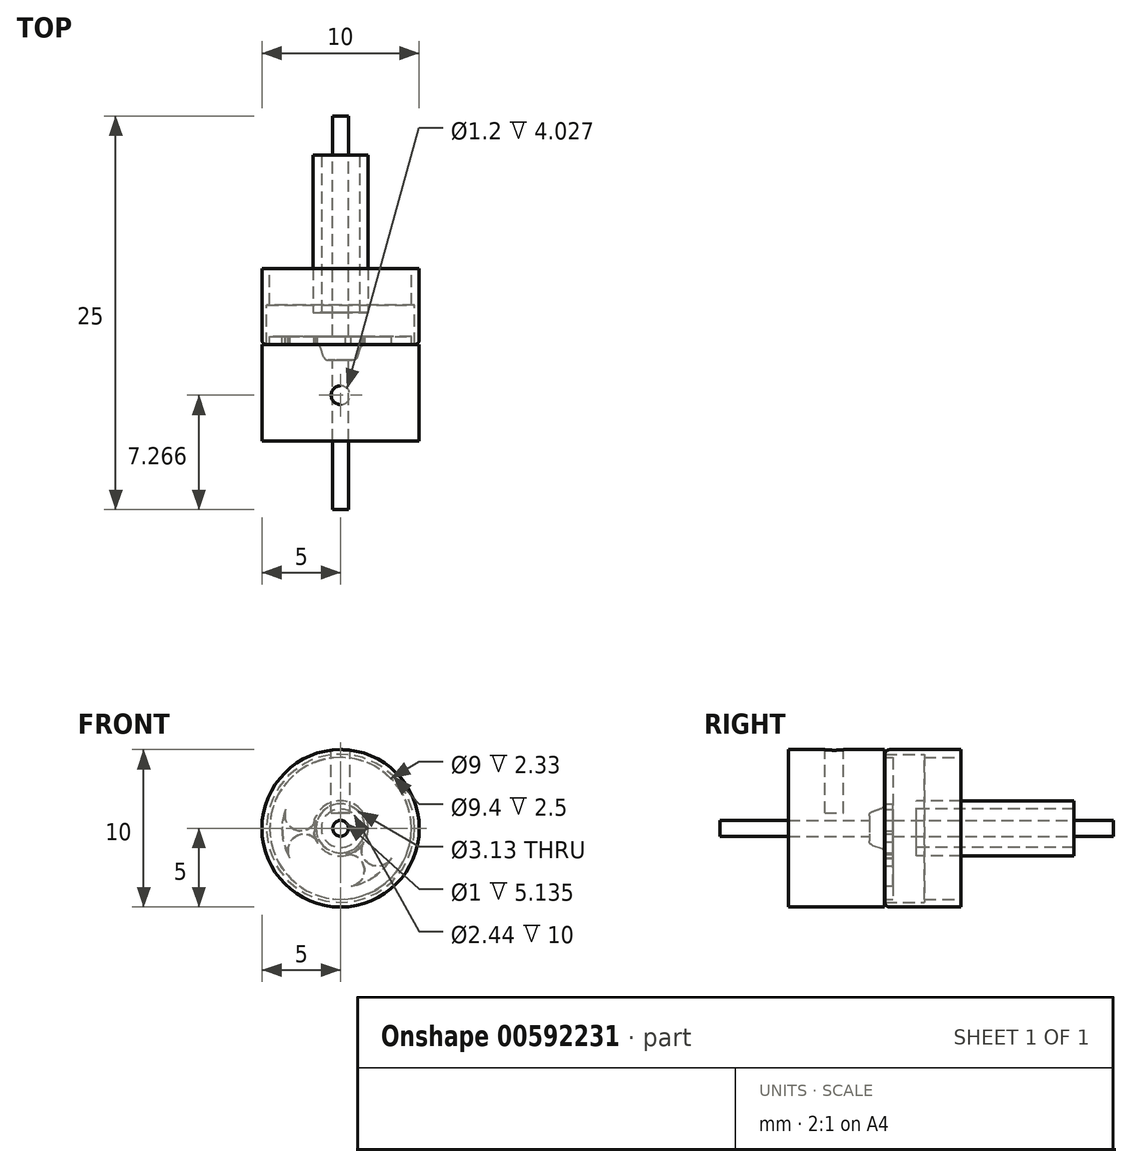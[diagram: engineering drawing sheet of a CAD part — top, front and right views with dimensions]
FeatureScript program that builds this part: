
annotation { "Feature Type Name" : "Feature", "Feature Type Description" : "" }
export const myFeature = defineFeature(function(context is Context, id is Id, definition is map)
    precondition{}
    {
        {
            var Q0;
            Q0=qCreatedBy(makeId("Right.planeOp"),FACE);
            var sketch = newSketch(context, id + "F0", { "sketchPlane" : qUnion([Q0])});
            skLineSegment(sketch, "E0", {"start": v(-3.01, 0) * mm, "end": v(-3.01, 1) * mm});
            skLineSegment(sketch, "E1", {"start": v(-3.01, 1) * mm, "end": v(-2.01, 1.35) * mm});
            skLineSegment(sketch, "E2", {"start": v(-2.01, 1.35) * mm, "end": v(-2.01, 5) * mm});
            skLineSegment(sketch, "E3", {"start": v(-2.01, 5) * mm, "end": v(2.82, 5) * mm});
            skLineSegment(sketch, "E4", {"start": v(2.82, 5) * mm, "end": v(2.82, 4.5) * mm});
            skLineSegment(sketch, "E5", {"start": v(2.82, 4.5) * mm, "end": v(-1.51, 4.5) * mm});
            skLineSegment(sketch, "E6", {"start": v(-1.51, 4.5) * mm, "end": v(-1.51, 0) * mm});
            skLineSegment(sketch, "E7", {"start": v(-1.51, 0) * mm, "end": v(-3.01, 0) * mm});
            skSolve(sketch);
        }
        {
            var Q0;
            Q0 = qSketchRegion(id + "F0", true);
            var Q1;
            Q1=sQuery(id+"F0.wireOp",EDGE,"E7");
            revolve(context, id + "F1", {"entities" : qUnion([Q0]), "axis" : qUnion([Q1]), "revolveType" : RevolveType.FULL});
        }
        {
            var Q0;
            Q0=makeQuery(id+"F1.opRevolve","SWEPT_EDGE",EDGE,{"disambiguationData":[OSD([sQuery(id+"F0.wireOp",EDGE,"E2"),sQuery(id+"F0.wireOp",EDGE,"E3")])]});
            var Q1;
            Q1=makeQuery(id+"F1.opRevolve","SWEPT_EDGE",EDGE,{"disambiguationData":[OSD([sQuery(id+"F0.wireOp",EDGE,"E1"),sQuery(id+"F0.wireOp",EDGE,"E2")])]});
            var Q2;
            Q2=makeQuery(id+"F1.opRevolve","SWEPT_EDGE",EDGE,{"disambiguationData":[OSD([sQuery(id+"F0.wireOp",EDGE,"E0"),sQuery(id+"F0.wireOp",EDGE,"E1")])]});
            fillet(context, id + "F2", {"entities" : qUnion([Q0, Q1, Q2]), "radius" : .3 * mm, "tangentPropagation" : true, "allowEdgeOverflow" : false});
        }
        {
            var Q0;
            Q0=makeQuery(id+"F1.opRevolve","SWEPT_FACE",FACE,{"disambiguationData":[OSD([sQuery(id+"F0.wireOp",EDGE,"E2")])]});
            var sketch = newSketch(context, id + "F3", { "sketchPlane" : qUnion([Q0])});
            skCircle(sketch, "E8", {"center": v(0, 2.66) * mm, "radius": 1.02 * mm});
            skCircle(sketch, "E9.1.0", {"center": v(2.04, 1.71) * mm, "radius": 1.02 * mm});
            skPoint(sketch, "E9.center", {"position": v(0, 0) * mm});
            skLineSegment(sketch, "E9.anchor1", {"start": v(0, 0) * mm, "end": v(0, 2.66) * mm, "construction": true});
            skLineSegment(sketch, "E9.anchor2", {"start": v(0, 0) * mm, "end": v(2.04, 1.71) * mm, "construction": true});
            skArc(sketch, "E10", {"start": v(0, 3.68) * mm, "mid": v(1.56, 3.34) * mm, "end": v(2.82, 2.37) * mm});
            skArc(sketch, "E11", {"start": v(0, 1.65) * mm, "mid": v(0.7, 1.5) * mm, "end": v(1.26, 1.06) * mm});
            skPoint(sketch, "E11.startSnap0", {"position": v(0, 1.33) * mm});
            skCircle(sketch, "E12.1.0", {"center": v(-2.33, -1.38) * mm, "radius": 1.02 * mm});
            skArc(sketch, "E12.1.1", {"start": v(-1.45, -0.88) * mm, "mid": v(-1.66, -0.2) * mm, "end": v(-1.57, 0.51) * mm});
            skCircle(sketch, "E12.1.2", {"center": v(-2.52, 0.86) * mm, "radius": 1.02 * mm});
            skLineSegment(sketch, "E12.1.3", {"start": v(-0.02, -0.05) * mm, "end": v(-2.33, -1.38) * mm, "construction": true});
            skArc(sketch, "E12.1.4", {"start": v(-3.2, -1.9) * mm, "mid": v(-3.69, -0.37) * mm, "end": v(-3.48, 1.2) * mm});
            skLineSegment(sketch, "E12.1.5", {"start": v(-0.02, -0.05) * mm, "end": v(-2.52, 0.86) * mm, "construction": true});
            skCircle(sketch, "E12.2.0", {"center": v(2.34, -1.38) * mm, "radius": 1.02 * mm});
            skArc(sketch, "E12.2.1", {"start": v(1.46, -0.87) * mm, "mid": v(0.98, -1.4) * mm, "end": v(0.32, -1.67) * mm});
            skCircle(sketch, "E12.2.2", {"center": v(0.5, -2.67) * mm, "radius": 1.02 * mm});
            skLineSegment(sketch, "E12.2.3", {"start": v(0.03, -0.04) * mm, "end": v(2.34, -1.38) * mm, "construction": true});
            skArc(sketch, "E12.2.4", {"start": v(3.22, -1.89) * mm, "mid": v(2.15, -3.06) * mm, "end": v(0.67, -3.67) * mm});
            skLineSegment(sketch, "E12.2.5", {"start": v(0.03, -0.04) * mm, "end": v(0.5, -2.67) * mm, "construction": true});
            skPoint(sketch, "E12.center", {"position": v(0, -0.03) * mm});
            skSolve(sketch);
        }
        {
            var Q0;
            {var subQ0=sQuery(id+"F3.wireOp",EDGE,"E8");var subQ1=makeQuery(id+"F3.imprint","INTERSECT",VERTEX,{"derivedFrom":[subQ0,sQuery(id+"F3.wireOp",EDGE,"E10")]});Q0=makeQuery(id+"F3.imprint","IMPRINT",FACE,{"disambiguationData":[TD([[makeQuery(id+"F3.imprint","IMPRINT",EDGE,{"disambiguationData":[TD([[subQ1,-1.0]])],"derivedFrom":subQ0}),1.0]])]});}
            var Q1;
            {var subQ0=sQuery(id+"F3.wireOp",EDGE,"E9.1.0");var subQ1=makeQuery(id+"F3.imprint","INTERSECT",VERTEX,{"derivedFrom":[subQ0,sQuery(id+"F3.wireOp",EDGE,"E10")]});Q1=makeQuery(id+"F3.imprint","IMPRINT",FACE,{"disambiguationData":[TD([[makeQuery(id+"F3.imprint","IMPRINT",EDGE,{"disambiguationData":[TD([[subQ1,-1.0]])],"derivedFrom":subQ0}),1.0]])]});}
            var Q2;
            {var subQ0=sQuery(id+"F3.wireOp",EDGE,"E12.1.0");var subQ1=makeQuery(id+"F3.imprint","INTERSECT",VERTEX,{"derivedFrom":[subQ0,sQuery(id+"F3.wireOp",EDGE,"E12.1.1")]});Q2=makeQuery(id+"F3.imprint","IMPRINT",FACE,{"disambiguationData":[TD([[makeQuery(id+"F3.imprint","IMPRINT",EDGE,{"disambiguationData":[TD([[subQ1,1.0]])],"derivedFrom":subQ0}),1.0]])]});}
            var Q3;
            {var subQ0=sQuery(id+"F3.wireOp",EDGE,"E12.1.2");var subQ1=makeQuery(id+"F3.imprint","INTERSECT",VERTEX,{"derivedFrom":[sQuery(id+"F3.wireOp",EDGE,"E12.1.1"),subQ0]});Q3=makeQuery(id+"F3.imprint","IMPRINT",FACE,{"disambiguationData":[TD([[makeQuery(id+"F3.imprint","IMPRINT",EDGE,{"disambiguationData":[TD([[subQ1,1.0]])],"derivedFrom":subQ0}),1.0]])]});}
            var Q4;
            {var subQ0=sQuery(id+"F3.wireOp",EDGE,"E12.2.0");var subQ1=makeQuery(id+"F3.imprint","INTERSECT",VERTEX,{"derivedFrom":[subQ0,sQuery(id+"F3.wireOp",EDGE,"E12.2.1")]});Q4=makeQuery(id+"F3.imprint","IMPRINT",FACE,{"disambiguationData":[TD([[makeQuery(id+"F3.imprint","IMPRINT",EDGE,{"disambiguationData":[TD([[subQ1,1.0]])],"derivedFrom":subQ0}),1.0]])]});}
            var Q5;
            {var subQ0=sQuery(id+"F3.wireOp",EDGE,"E12.2.2");var subQ1=makeQuery(id+"F3.imprint","INTERSECT",VERTEX,{"derivedFrom":[sQuery(id+"F3.wireOp",EDGE,"E12.2.1"),subQ0]});Q5=makeQuery(id+"F3.imprint","IMPRINT",FACE,{"disambiguationData":[TD([[makeQuery(id+"F3.imprint","IMPRINT",EDGE,{"disambiguationData":[TD([[subQ1,1.0]])],"derivedFrom":subQ0}),1.0]])]});}
            var Q6;
            {var subQ0=sQuery(id+"F3.wireOp",EDGE,"E12.1.1");Q6=makeQuery(id+"F3.imprint","IMPRINT",FACE,{"disambiguationData":[TD([[makeQuery(id+"F3.imprint","IMPRINT",EDGE,{"derivedFrom":subQ0}),1.0]])]});}
            var Q7;
            {var subQ0=sQuery(id+"F3.wireOp",EDGE,"E12.2.1");Q7=makeQuery(id+"F3.imprint","IMPRINT",FACE,{"disambiguationData":[TD([[makeQuery(id+"F3.imprint","IMPRINT",EDGE,{"derivedFrom":subQ0}),1.0]])]});}
            var Q8;
            {var subQ0=sQuery(id+"F3.wireOp",EDGE,"E11");var subQ1=sQuery(id+"F3.wireOp",EDGE,"E8");var subQ2=makeQuery(id+"F3.imprint","INTERSECT",VERTEX,{"derivedFrom":[subQ1,subQ0]});Q8=makeQuery(id+"F3.imprint","IMPRINT",FACE,{"disambiguationData":[TD([[makeQuery(id+"F3.imprint","IMPRINT",EDGE,{"disambiguationData":[TD([[subQ2,-1.0]])],"derivedFrom":subQ1}),-1.0]])]});}
            var Q9;
            {var subQ0=sQuery(id+"F3.wireOp",EDGE,"2b185309-59a0-4bb1-aa12-8d7028a0172f.2.4.0");var subQ1=sQuery(id+"F3.wireOp",EDGE,"2b185309-59a0-4bb1-aa12-8d7028a0172f.1.4.0");var subQ2=makeQuery(id+"F3.imprint","INTERSECT",VERTEX,{"derivedFrom":[subQ1,subQ0]});Q9=makeQuery(id+"F3.imprint","IMPRINT",FACE,{"disambiguationData":[TD([[makeQuery(id+"F3.imprint","IMPRINT",EDGE,{"disambiguationData":[TD([[subQ2,-1.0]])],"derivedFrom":subQ1}),-1.0]])]});}
            var Q10;
            {var subQ1=sQuery(id+"F3.wireOp",EDGE,"2b185309-59a0-4bb1-aa12-8d7028a0172f.1.4.0");var subQ3=makeQuery(id+"F3.imprint","IMPRINT",VERTEX,{"derivedFrom":subQ1});Q10=makeQuery(id+"F3.imprint","IMPRINT",FACE,{"disambiguationData":[TD([[makeQuery(id+"F3.imprint","IMPRINT",EDGE,{"disambiguationData":[TD([[subQ3,1.0]])],"derivedFrom":subQ1}),1.0]])]});}
            var Q11;
            {var subQ0=sQuery(id+"F3.wireOp",EDGE,"2b185309-59a0-4bb1-aa12-8d7028a0172f.6.4.0");var subQ1=makeQuery(id+"F3.imprint","INTERSECT",VERTEX,{"derivedFrom":[sQuery(id+"F3.wireOp",EDGE,"2b185309-59a0-4bb1-aa12-8d7028a0172f.2.4.0"),subQ0]});Q11=makeQuery(id+"F3.imprint","IMPRINT",FACE,{"disambiguationData":[TD([[makeQuery(id+"F3.imprint","IMPRINT",EDGE,{"disambiguationData":[TD([[subQ1,1.0]])],"derivedFrom":subQ0}),1.0]])]});}
            var Q12;
            {var subQ1=sQuery(id+"F3.wireOp",EDGE,"0a5dfd87-6915-47c6-89d9-1c4287bb2b64.1.3.0");var subQ3=makeQuery(id+"F3.imprint","IMPRINT",VERTEX,{"derivedFrom":subQ1});Q12=makeQuery(id+"F3.imprint","IMPRINT",FACE,{"disambiguationData":[TD([[makeQuery(id+"F3.imprint","IMPRINT",EDGE,{"disambiguationData":[TD([[subQ3,1.0]])],"derivedFrom":subQ1}),1.0]])]});}
            var Q13;
            {var subQ0=sQuery(id+"F3.wireOp",EDGE,"0a5dfd87-6915-47c6-89d9-1c4287bb2b64.2.3.0");var subQ1=sQuery(id+"F3.wireOp",EDGE,"0a5dfd87-6915-47c6-89d9-1c4287bb2b64.1.3.0");var subQ2=makeQuery(id+"F3.imprint","INTERSECT",VERTEX,{"derivedFrom":[subQ1,subQ0]});Q13=makeQuery(id+"F3.imprint","IMPRINT",FACE,{"disambiguationData":[TD([[makeQuery(id+"F3.imprint","IMPRINT",EDGE,{"disambiguationData":[TD([[subQ2,-1.0]])],"derivedFrom":subQ1}),-1.0]])]});}
            var Q14;
            {var subQ0=sQuery(id+"F3.wireOp",EDGE,"0a5dfd87-6915-47c6-89d9-1c4287bb2b64.6.3.0");var subQ1=makeQuery(id+"F3.imprint","INTERSECT",VERTEX,{"derivedFrom":[sQuery(id+"F3.wireOp",EDGE,"0a5dfd87-6915-47c6-89d9-1c4287bb2b64.2.3.0"),subQ0]});Q14=makeQuery(id+"F3.imprint","IMPRINT",FACE,{"disambiguationData":[TD([[makeQuery(id+"F3.imprint","IMPRINT",EDGE,{"disambiguationData":[TD([[subQ1,1.0]])],"derivedFrom":subQ0}),1.0]])]});}
            var Q15;
            {var subQ0=sQuery(id+"F3.wireOp",EDGE,"E9.1.0");var subQ1=makeQuery(id+"F3.imprint","INTERSECT",VERTEX,{"derivedFrom":[subQ0,sQuery(id+"F3.wireOp",EDGE,"E11")]});Q15=makeQuery(id+"F3.imprint","IMPRINT",FACE,{"disambiguationData":[TD([[makeQuery(id+"F3.imprint","IMPRINT",EDGE,{"disambiguationData":[TD([[subQ1,1.0]])],"derivedFrom":subQ0}),1.0]])]});}
            var Q16;
            {var subQ1=sQuery(id+"F3.wireOp",EDGE,"E8");var subQ3=makeQuery(id+"F3.imprint","IMPRINT",VERTEX,{"derivedFrom":subQ1});Q16=makeQuery(id+"F3.imprint","IMPRINT",FACE,{"disambiguationData":[TD([[makeQuery(id+"F3.imprint","IMPRINT",EDGE,{"disambiguationData":[TD([[subQ3,1.0]])],"derivedFrom":subQ1}),1.0]])]});}
            extrude(context, id + "F4", {"entities" : qUnion([Q0, Q1, Q2, Q3, Q4, Q5, Q6, Q7, Q8, Q9, Q10, Q11, Q12, Q13, Q14, Q15, Q16]), "operationType" : NewBodyOperationType.REMOVE, "endBound" : BoundingType.SYMMETRIC, "depth" : 5 * mm, "offsetDistance" : 25 * mm});
        }
        {
            var Q0;
            Q0=qCreatedBy(makeId("Front.planeOp"),FACE);
            var sketch = newSketch(context, id + "F5", { "sketchPlane" : qUnion([Q0])});
            skCircle(sketch, "E13", {"center": v(0, 0) * mm, "radius": 0.5 * mm});
            skCircle(sketch, "E14", {"center": v(0, 0) * mm, "radius": 1.75 * mm});
            skCircle(sketch, "E15", {"center": v(0, 0) * mm, "radius": 1.22 * mm});
            skSolve(sketch);
        }
        {
            var Q0;
            Q0=makeQuery(id+"F5.imprint","IMPRINT",FACE,{"disambiguationData":[TD([[makeQuery(id+"F5.imprint","IMPRINT",EDGE,{"derivedFrom":sQuery(id+"F5.wireOp",EDGE,"E14")}),1.0]])]});
            extrude(context, id + "F6", {"entities" : qUnion([Q0]), "operationType" : NewBodyOperationType.ADD, "depth" : -10 * mm, "offsetDistance" : 25 * mm});
        }
        {
            var Q0;
            Q0=makeQuery(id+"F5.imprint","IMPRINT",FACE,{"disambiguationData":[TD([[makeQuery(id+"F5.imprint","IMPRINT",EDGE,{"derivedFrom":sQuery(id+"F5.wireOp",EDGE,"E13")}),1.0]])]});
            extrude(context, id + "F7", {"entities" : qUnion([Q0]), "operationType" : NewBodyOperationType.ADD, "endBound" : BoundingType.SYMMETRIC, "depth" : 25 * mm, "offsetDistance" : 25 * mm});
        }
        {
            var Q0;
            Q0=qCreatedBy(makeId("Right.planeOp"),FACE);
            var sketch = newSketch(context, id + "F8", { "sketchPlane" : qUnion([Q0])});
            skLineSegment(sketch, "E16", {"start": v(-3.81, 0) * mm, "end": v(-16.52, 0) * mm, "construction": true});
            skLineSegment(sketch, "E17", {"start": v(-1.51, 0) * mm, "end": v(-1.51, 4.5) * mm});
            skLineSegment(sketch, "E18", {"start": v(-1.51, 4.5) * mm, "end": v(-2.03, 4.5) * mm});
            skLineSegment(sketch, "E19", {"start": v(-2.03, 4.5) * mm, "end": v(-2.03, 5) * mm});
            skLineSegment(sketch, "E20", {"start": v(-2.03, 5) * mm, "end": v(-8.15, 5) * mm});
            skLineSegment(sketch, "E21", {"start": v(-8.15, 5) * mm, "end": v(-8.15, 0) * mm});
            skLineSegment(sketch, "E22", {"start": v(-8.15, 0) * mm, "end": v(-1.51, 0) * mm});
            skLineSegment(sketch, "E23", {"start": v(-5.83, 5) * mm, "end": v(-5.83, 0.97) * mm});
            skLineSegment(sketch, "E24", {"start": v(-5.83, 0.97) * mm, "end": v(-5.23, 0.97) * mm});
            skLineSegment(sketch, "E25", {"start": v(-5.23, 0.97) * mm, "end": v(-5.23, 5) * mm});
            skSolve(sketch);
        }
        {
            var Q0;
            Q0=makeQuery(id+"F8.imprint","IMPRINT",FACE,{"disambiguationData":[TD([[makeQuery(id+"F8.imprint","IMPRINT",EDGE,{"derivedFrom":sQuery(id+"F8.wireOp",EDGE,"E17")}),1.0]])]});
            var Q1;
            {var subQ0=sQuery(id+"F8.wireOp",EDGE,"E23");Q1=makeQuery(id+"F8.imprint","IMPRINT",FACE,{"disambiguationData":[TD([[makeQuery(id+"F8.imprint","IMPRINT",EDGE,{"derivedFrom":subQ0}),1.0]])]});}
            var Q2;
            Q2=sQuery(id+"F8.wireOp",EDGE,"E16");
            revolve(context, id + "F9", {"entities" : qUnion([Q0, Q1]), "axis" : qUnion([Q2]), "revolveType" : RevolveType.FULL});
        }
        {
            var Q0;
            {var subQ0=sQuery(id+"F8.wireOp",EDGE,"E23");Q0=makeQuery(id+"F8.imprint","IMPRINT",FACE,{"disambiguationData":[TD([[makeQuery(id+"F8.imprint","IMPRINT",EDGE,{"derivedFrom":subQ0}),1.0]])]});}
            var Q1;
            Q1=sQuery(id+"F8.wireOp",EDGE,"E25");
            revolve(context, id + "F10", {"operationType" : NewBodyOperationType.REMOVE, "entities" : qUnion([Q0]), "axis" : qUnion([Q1]), "revolveType" : RevolveType.FULL, "oppositeDirection" : true});
        }
        {
            var Q0;
            Q0=makeQuery(id+"F1.opRevolve","SWEPT_BODY",BODY,{"disambiguationData":[OSD([sQuery(id+"F0.wireOp",EDGE,"E0"),sQuery(id+"F0.wireOp",EDGE,"E1"),sQuery(id+"F0.wireOp",EDGE,"E2"),sQuery(id+"F0.wireOp",EDGE,"E3"),sQuery(id+"F0.wireOp",EDGE,"E4"),sQuery(id+"F0.wireOp",EDGE,"E5"),sQuery(id+"F0.wireOp",EDGE,"E6"),sQuery(id+"F0.wireOp",EDGE,"E7")])]});
            var Q1;
            Q1=makeQuery(id+"F9.opRevolve","SWEPT_BODY",BODY,{"disambiguationData":[OSD([sQuery(id+"F8.wireOp",EDGE,"E17"),sQuery(id+"F8.wireOp",EDGE,"E18"),sQuery(id+"F8.wireOp",EDGE,"E19"),sQuery(id+"F8.wireOp",EDGE,"E20"),sQuery(id+"F8.wireOp",EDGE,"E21"),sQuery(id+"F8.wireOp",EDGE,"E22")])]});
            booleanBodies(context, id + "F11", {"operationType" : BooleanOperationType.SUBTRACTION, "tools" : qUnion([Q0]), "targets" : qUnion([Q1]), "keepTools" : true});
        }
    });
